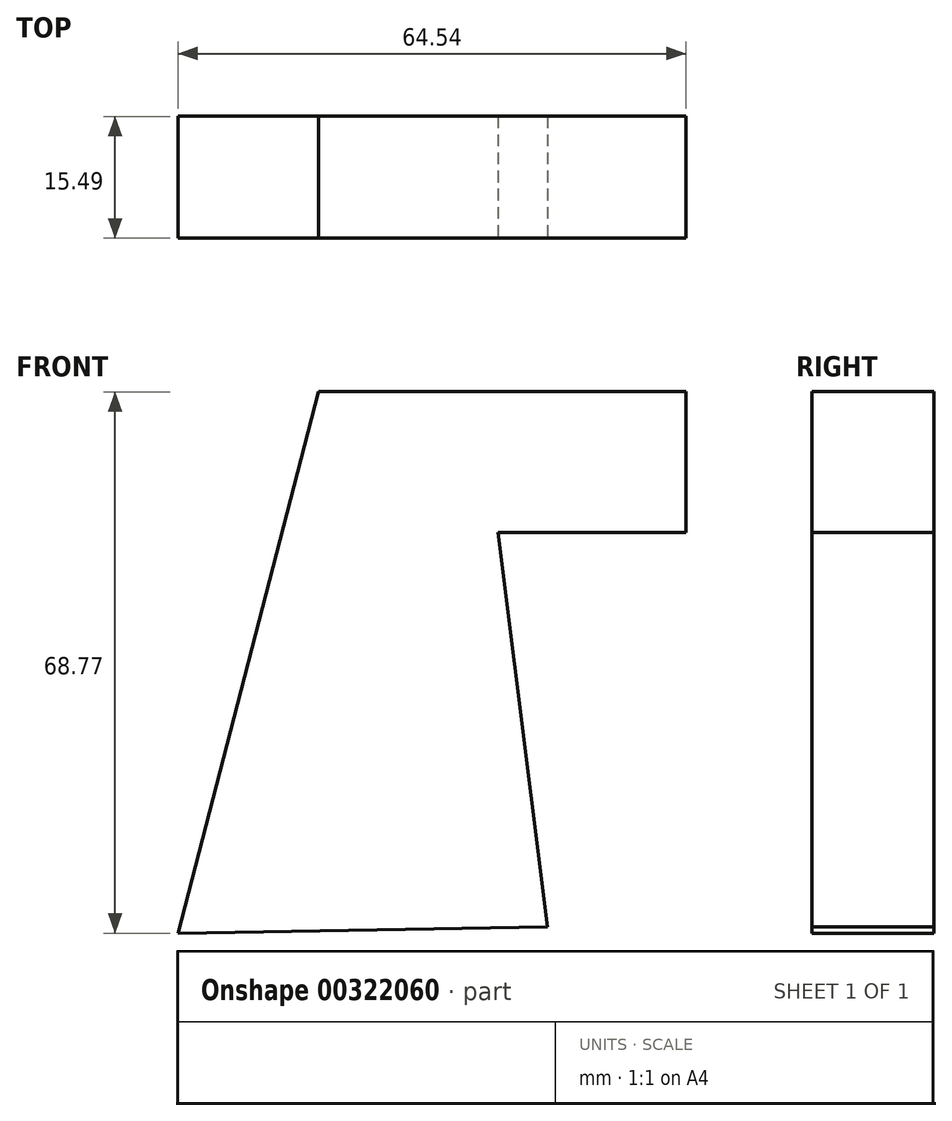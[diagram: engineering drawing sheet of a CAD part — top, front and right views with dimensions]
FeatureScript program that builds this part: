
annotation { "Feature Type Name" : "Feature", "Feature Type Description" : "" }
export const myFeature = defineFeature(function(context is Context, id is Id, definition is map)
    precondition{}
    {
        {
            var Q0;
            Q0=qCreatedBy(makeId("Front.planeOp"),FACE);
            var sketch = newSketch(context, id + "F0", { "sketchPlane" : qUnion([Q0])});
            skLineSegment(sketch, "E0", {"start": v(-52, -38.11) * mm, "end": v(-34.17, 30.66) * mm});
            skLineSegment(sketch, "E1", {"start": v(-34.17, 30.66) * mm, "end": v(-13.62, 30.66) * mm});
            skLineSegment(sketch, "E2", {"start": v(-13.62, 30.66) * mm, "end": v(-5.04, -37.33) * mm});
            skLineSegment(sketch, "E3", {"start": v(-52, -38.11) * mm, "end": v(-5.04, -37.33) * mm});
            skLineSegment(sketch, "E4", {"start": v(-13.62, 30.66) * mm, "end": v(12.55, 30.66) * mm});
            skPoint(sketch, "E4.endSnap0", {"position": v(-23.9, 30.66) * mm});
            skLineSegment(sketch, "E5", {"start": v(12.55, 30.66) * mm, "end": v(12.55, 12.82) * mm});
            skLineSegment(sketch, "E6", {"start": v(12.55, 12.82) * mm, "end": v(-11.37, 12.82) * mm});
            skLineSegment(sketch, "E7", {"start": v(-9.38, 14.17) * mm, "end": v(-11.37, 12.82) * mm});
            skSolve(sketch);
        }
        {
            var Q0;
            Q0 = qSketchRegion(id + "F0", true);
            extrude(context, id + "F1", {"entities" : qUnion([Q0]), "oppositeDirection" : true, "depth" : 15.5 * mm});
        }
    });
